# Revit family: RM-15
name_source: partatom
category: Plumbing Fixtures
revit_build: Autodesk Revit 2014 (Build: 20130308_1515(x64)
units: mm (PartAtom-declared; Revit-internal decimal feet)

## types (1)
- RM-15
    Brass Chromed = Brass
    Data Sheet = http://helvex.com
    Description = Square Hand Shower With Deflecting For Width Plate
    Features = Shower Medium And High Pressure; Hand Shower With Dynamic Economizer Water; Recessed Fixture; Includes Setting Kit; Hand Shower Diverter Or Fixed Jet; Length Hose 59" (1,5 m)
    Inlet Threads = ½" - 14 NPT
    Instructive = http://helvex.com
    Manufacturer = HELVEX
    Max. Water Flow = 2.6 gal/min
    Max. Working Pressure = 85.3 psi
    Min. Water Flow = 1.1 gal/min
    Min. Working Pressure = 14.2 psi
    Model = RM-15
    Niquel Duravex = Niquel Duravex
    Plastic Showerhead = Plastic
    Satin = Satin Duravex
    Total Depth = 14"
    Total Width = 8"
    Type Comments = Hand Shower
    URL = http://helvex.com

## geometry (parser evidence)
native form markers: Sweep x1
no freeform markers — native parametric forms only
